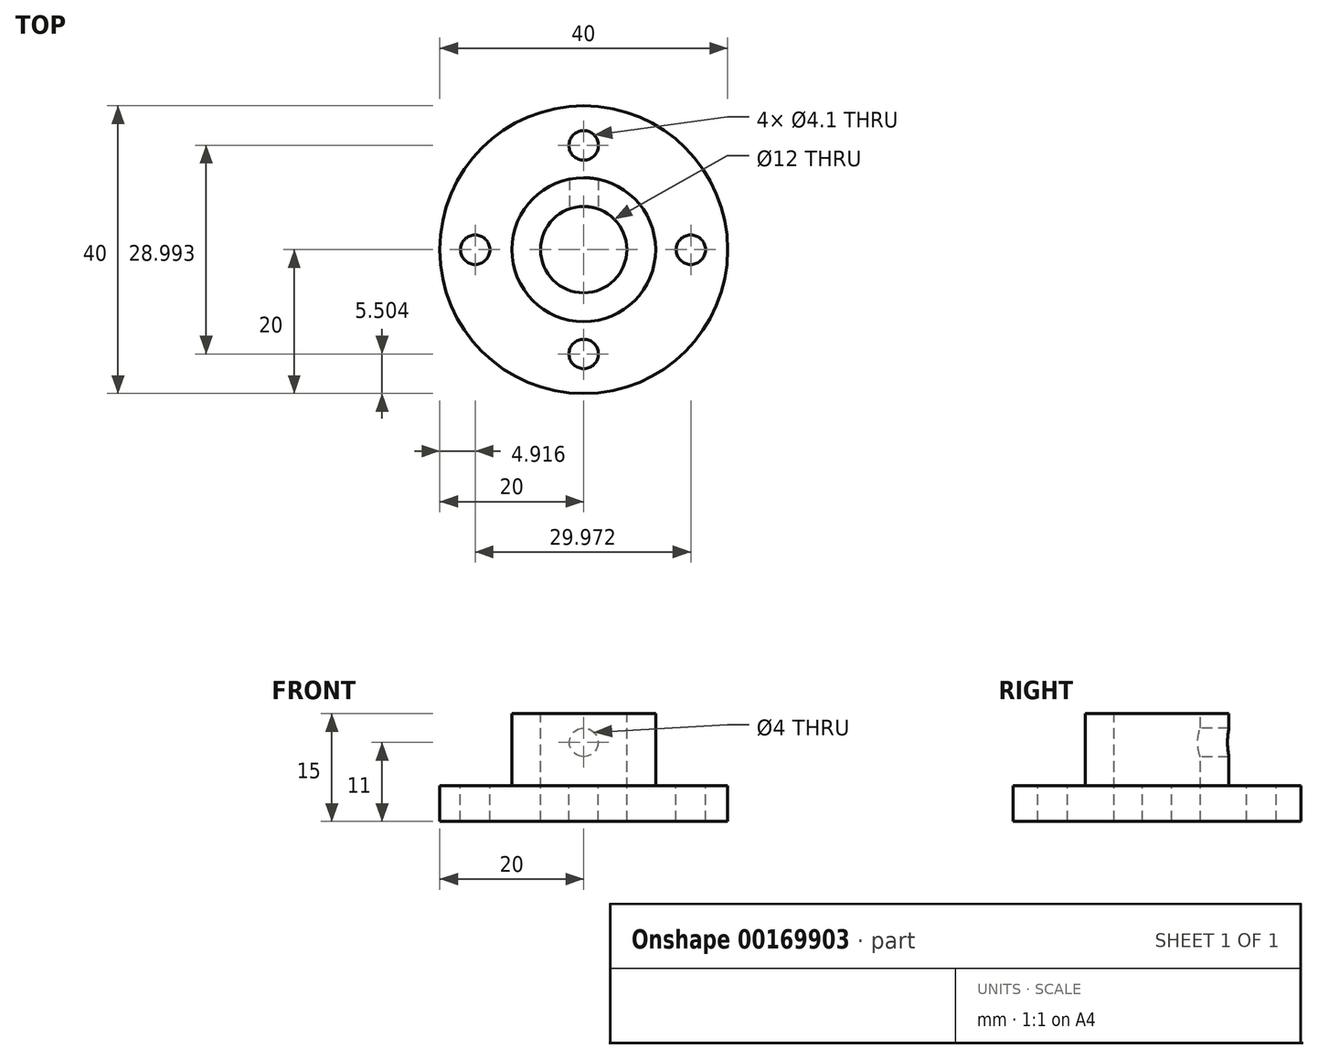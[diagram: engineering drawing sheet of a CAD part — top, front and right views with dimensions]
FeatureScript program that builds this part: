
annotation { "Feature Type Name" : "Feature", "Feature Type Description" : "" }
export const myFeature = defineFeature(function(context is Context, id is Id, definition is map)
    precondition{}
    {
        {
            var Q0;
            Q0=qCreatedBy(makeId("Front.planeOp"),FACE);
            var sketch = newSketch(context, id + "F0", { "sketchPlane" : qUnion([Q0])});
            skLineSegment(sketch, "E0", {"start": v(0, 0) * mm, "end": v(-10, 0) * mm});
            skLineSegment(sketch, "E1", {"start": v(-10, 0) * mm, "end": v(-10, -10) * mm});
            skLineSegment(sketch, "E2", {"start": v(-10, -10) * mm, "end": v(-20, -10) * mm});
            skLineSegment(sketch, "E3", {"start": v(-20, -10) * mm, "end": v(-20, -15) * mm});
            skLineSegment(sketch, "E4", {"start": v(-20, -15) * mm, "end": v(0, -15) * mm});
            skLineSegment(sketch, "E5", {"start": v(0, 0) * mm, "end": v(0, -15) * mm});
            skSolve(sketch);
        }
        {
            var Q0;
            Q0=makeQuery(id+"F0.imprint","IMPRINT",FACE,{"disambiguationData":[TD([[makeQuery(id+"F0.imprint","IMPRINT",EDGE,{"derivedFrom":sQuery(id+"F0.wireOp",EDGE,"E0")}),1.0]])]});
            var Q1;
            Q1=sQuery(id+"F0.wireOp",EDGE,"E5");
            revolve(context, id + "F1", {"entities" : qUnion([Q0]), "axis" : qUnion([Q1]), "revolveType" : RevolveType.FULL});
        }
        {
            var Q0;
            Q0=makeQuery(id+"F1.opRevolve","SWEPT_FACE",FACE,{"disambiguationData":[OSD([sQuery(id+"F0.wireOp",EDGE,"E0")])]});
            var sketch = newSketch(context, id + "F2", { "sketchPlane" : qUnion([Q0])});
            skCircle(sketch, "E6", {"center": v(0, 0) * mm, "radius": 6 * mm});
            skSolve(sketch);
        }
        {
            var Q0;
            Q0=makeQuery(id+"F2.imprint","IMPRINT",FACE,{"disambiguationData":[TD([[makeQuery(id+"F2.imprint","IMPRINT",EDGE,{"derivedFrom":sQuery(id+"F2.wireOp",EDGE,"E6")}),1.0]])]});
            extrude(context, id + "F3", {"entities" : qUnion([Q0]), "operationType" : NewBodyOperationType.REMOVE, "oppositeDirection" : true, "depth" : 45 * mm});
        }
        {
            var Q0;
            Q0=qCreatedBy(makeId("Top.planeOp"),FACE);
            var sketch = newSketch(context, id + "F4", { "sketchPlane" : qUnion([Q0])});
            skCircle(sketch, "E7", {"center": v(0, 14.5) * mm, "radius": 2.05 * mm});
            skCircle(sketch, "E8", {"center": v(0, -14.5) * mm, "radius": 2.05 * mm});
            skCircle(sketch, "E9", {"center": v(14.89, 0) * mm, "radius": 2.05 * mm});
            skCircle(sketch, "E10", {"center": v(-15.08, 0) * mm, "radius": 2.05 * mm});
            skSolve(sketch);
        }
        {
            var Q0;
            Q0 = qSketchRegion(id + "F4", true);
            extrude(context, id + "F5", {"entities" : qUnion([Q0]), "operationType" : NewBodyOperationType.REMOVE, "oppositeDirection" : true, "depth" : 25 * mm});
        }
        {
            var Q0;
            Q0=qCreatedBy(makeId("Front.planeOp"),FACE);
            var sketch = newSketch(context, id + "F6", { "sketchPlane" : qUnion([Q0])});
            skCircle(sketch, "E11", {"center": v(0, -4) * mm, "radius": 2 * mm});
            skSolve(sketch);
        }
        {
            var Q0;
            Q0 = qSketchRegion(id + "F6", true);
            extrude(context, id + "F7", {"entities" : qUnion([Q0]), "operationType" : NewBodyOperationType.REMOVE, "oppositeDirection" : true, "depth" : 10 * mm});
        }
    });
